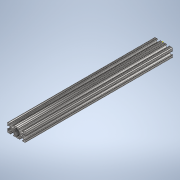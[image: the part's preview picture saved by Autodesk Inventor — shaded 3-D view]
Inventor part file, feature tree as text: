
AUTODESK INVENTOR PART (.ipt)
format: ipt  version: 2020 (Build 240168000, 168)  size: 348,160 bytes
history: native  units: in
note: dims shown in document units (in); Inventor stores cm internally (conversion verified against a paired STEP export)
features: sketch x2, extrude x1
ambient origin geometry x8: Origin, YZ Plane, XZ Plane, XY Plane, X Axis, Y Axis, Z Axis, Center Point
bodies: Solid1 (feature_tree)
feature tree (3):
  extrude  "Extrusion1"  [1 undecoded]
  sketch  "Sketch2"
  sketch  "Sketch1"  dims[d0=16.0in d1=0.0in]
note: 1 required parameter value undecoded (feature->parameter linkage not recoverable at this tier; creation-order binding heuristic only, values carry confidence <= 0.55)
